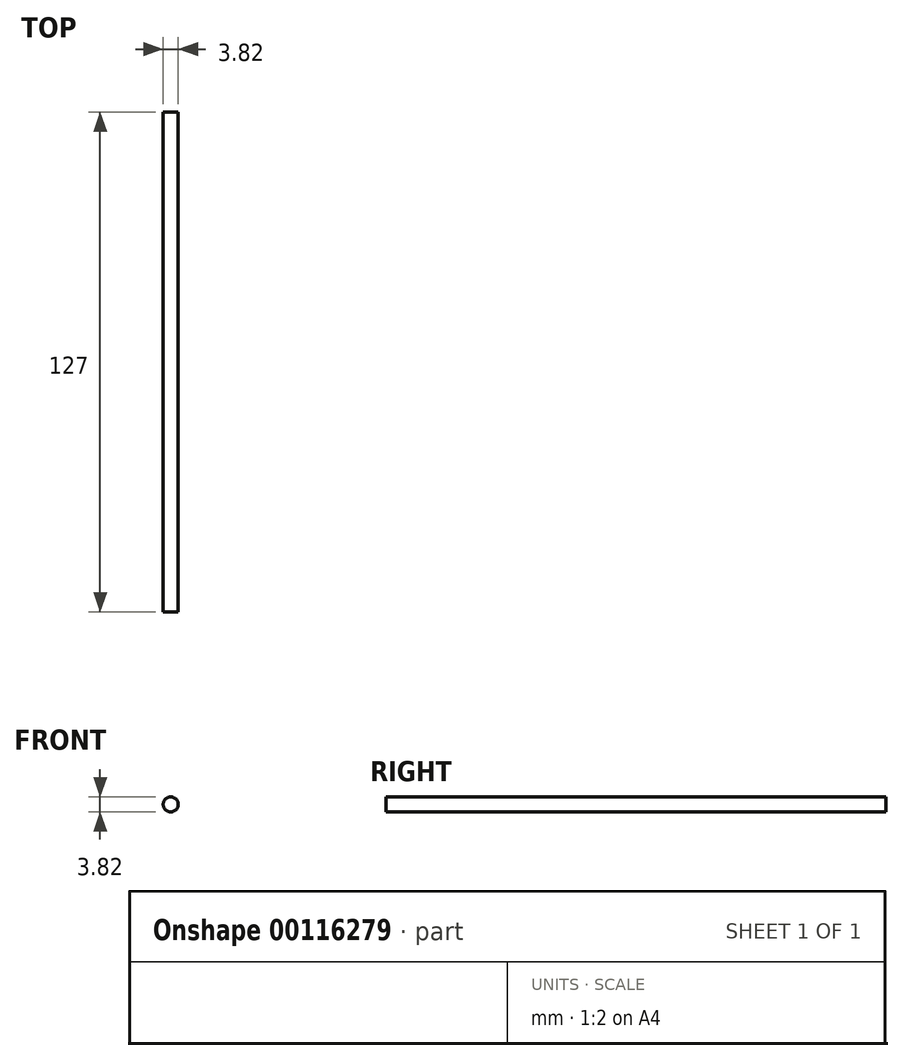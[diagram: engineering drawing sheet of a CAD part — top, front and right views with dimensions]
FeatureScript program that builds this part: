
annotation { "Feature Type Name" : "Feature", "Feature Type Description" : "" }
export const myFeature = defineFeature(function(context is Context, id is Id, definition is map)
    precondition{}
    {
        {
            var Q0;
            Q0=qCreatedBy(makeId("Front.planeOp"),FACE);
            var sketch = newSketch(context, id + "F0", { "sketchPlane" : qUnion([Q0])});
            skCircle(sketch, "E0", {"center": v(0, 0) * mm, "radius": 1.9 * mm});
            skSolve(sketch);
        }
        {
            var Q0;
            Q0 = qSketchRegion(id + "F0", true);
            extrude(context, id + "F1", {"entities" : qUnion([Q0]), "depth" : 101.6 * mm});
        }
        {
            var Q0;
            Q0=makeQuery(id+"F1.opExtrude","CAP_FACE",FACE,{"disambiguationData":[OSD([sQuery(id+"F0.wireOp",EDGE,"E0")])],"isStart":true});
            extrude(context, id + "F2", {"entities" : qUnion([Q0]), "operationType" : NewBodyOperationType.ADD, "depth" : 25.4 * mm});
        }
    });
